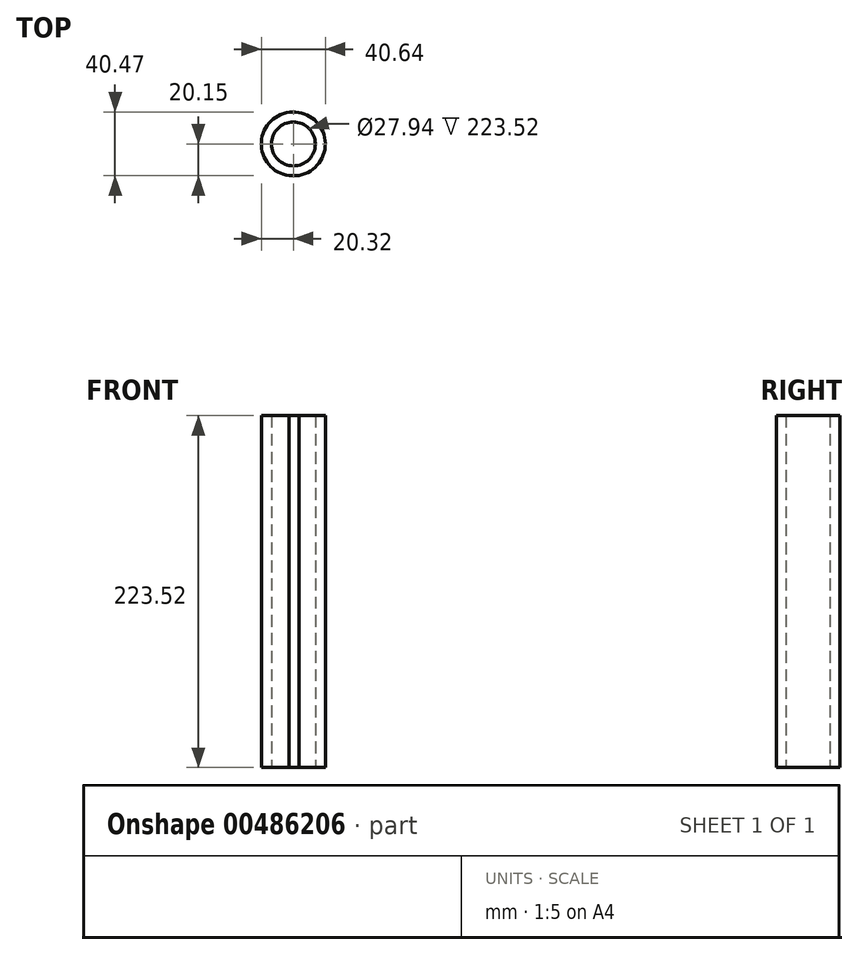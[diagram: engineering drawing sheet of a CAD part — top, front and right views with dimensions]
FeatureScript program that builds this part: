
annotation { "Feature Type Name" : "Feature", "Feature Type Description" : "" }
export const myFeature = defineFeature(function(context is Context, id is Id, definition is map)
    precondition{}
    {
        {
            var Q0;
            Q0=qCreatedBy(makeId("Top.planeOp"),FACE);
            var sketch = newSketch(context, id + "F0", { "sketchPlane" : qUnion([Q0])});
            skCircle(sketch, "E0", {"center": v(0, 0) * mm, "radius": 13.97 * mm});
            skCircle(sketch, "E1", {"center": v(0, 0) * mm, "radius": 20.32 * mm});
            skLineSegment(sketch, "E2", {"start": v(-2.6, -20.15) * mm, "end": v(3.74, -19.97) * mm});
            skLineSegment(sketch, "E3", {"start": v(-2.6, -20.15) * mm, "end": v(-2.6, -20.18) * mm});
            skLineSegment(sketch, "E4", {"start": v(-2.6, -20.18) * mm, "end": v(3.74, -20.15) * mm});
            skSolve(sketch);
        }
        {
            var Q0;
            Q0=makeQuery(id+"F0.imprint","IMPRINT",FACE,{"disambiguationData":[TD([[makeQuery(id+"F0.imprint","IMPRINT",EDGE,{"derivedFrom":sQuery(id+"F0.wireOp",EDGE,"E0")}),-1.0]])]});
            extrude(context, id + "F1", {"entities" : qUnion([Q0]), "depth" : 223.52 * mm, "offsetDistance" : 25.4 * mm});
        }
    });
